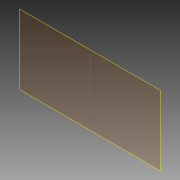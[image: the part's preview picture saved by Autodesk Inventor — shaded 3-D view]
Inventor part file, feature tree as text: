
AUTODESK INVENTOR PART (.ipt)
format: ipt  version: 2013 (Build 170138000, 138)  size: 71,168 bytes
history: native  units: in
note: dims shown in document units (in); Inventor stores cm internally (conversion verified against a paired STEP export)
features: plane x1, extrude x1, sketch x1, reference x1
ambient origin geometry x8: Origin, YZ Plane, XZ Plane, XY Plane, X Axis, Y Axis, Z Axis, Center Point
bodies: Solid1 (feature_tree)
feature tree (4):
  plane  "Work Plane1"
  extrude  "Extrusion1"  Depth=0.1in TaperAngle=0.0deg
  sketch  "Sketch1"  dims[d0=2.0in d2=0.1in d3=0.0in]
  reference  "Reference1"
